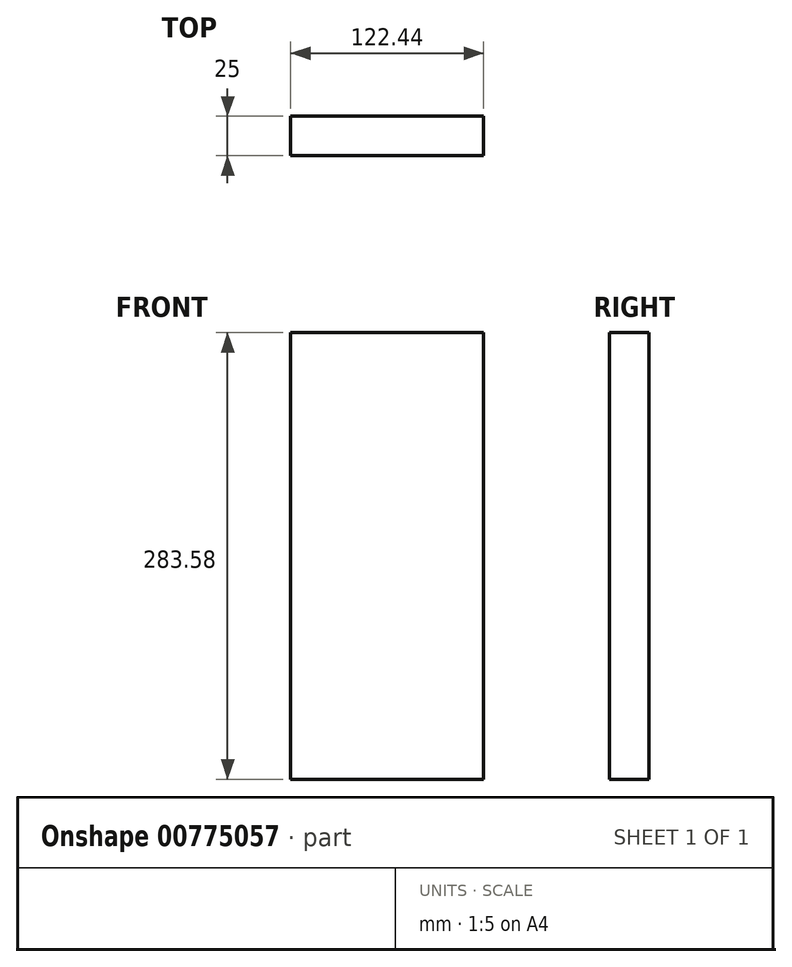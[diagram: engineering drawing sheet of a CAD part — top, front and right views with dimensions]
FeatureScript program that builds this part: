
annotation { "Feature Type Name" : "Feature", "Feature Type Description" : "" }
export const myFeature = defineFeature(function(context is Context, id is Id, definition is map)
    precondition{}
    {
        {
            var Q0;
            Q0=qCreatedBy(makeId("Front.planeOp"), FACE);
            var sketch = newSketch(context, id + "F0", { "sketchPlane" : qUnion([Q0])});
            skLineSegment(sketch, "E0.bottom", {"start": v(61.22, 141.79) * mm, "end": v(-61.22, 141.79) * mm});
            skLineSegment(sketch, "E0.top", {"start": v(61.22, -141.79) * mm, "end": v(-61.22, -141.79) * mm});
            skLineSegment(sketch, "E0.left", {"start": v(61.22, 141.79) * mm, "end": v(61.22, -141.79) * mm});
            skLineSegment(sketch, "E0.right", {"start": v(-61.22, 141.79) * mm, "end": v(-61.22, -141.79) * mm});
            skPoint(sketch, "E0.middle", {"position": v(0, 0) * mm});
            skSolve(sketch);
        }
        {
            var Q0;
            Q0 = qSketchRegion(id + "F0", true);
            extrude(context, id + "F1", {"entities" : qUnion([Q0]), "domain" : OperationDomain.MODEL, "flatOperationType" : FlatOperationType.REMOVE, "depth" : 25 * mm, "offsetDistance" : 25 * mm});
        }
    });
